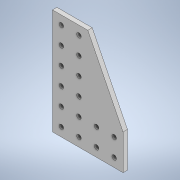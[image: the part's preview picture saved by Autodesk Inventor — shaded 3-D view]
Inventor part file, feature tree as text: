
AUTODESK INVENTOR PART (.ipt)
format: ipt  version: 2020 (Build 240168000, 168)  size: 137,216 bytes
history: native  units: in
note: dims shown in document units (in); Inventor stores cm internally (conversion verified against a paired STEP export)
features: extrude x1, sketch x1
ambient origin geometry x8: Origin, YZ Plane, XZ Plane, XY Plane, X Axis, Y Axis, Z Axis, Center Point
bodies: Solid1 (feature_tree)
feature tree (2):
  extrude  "Extrusion1"  Depth=0.25in
  sketch  "Sketch1"  dims[d6=4.0in d7=2.0in d8=2.0in d9=4.0in d10=2.0in d11=4.0in d12=2.0in d13=0.256in d14=0.5in d15=0.5in d16=2.3622in d18=1.0in d19=0.7874in d21=1.0in d24=1.1811in d26=1.0in d27=0.7874in d29=1.0in d32=0.25in d33=0.0in]
